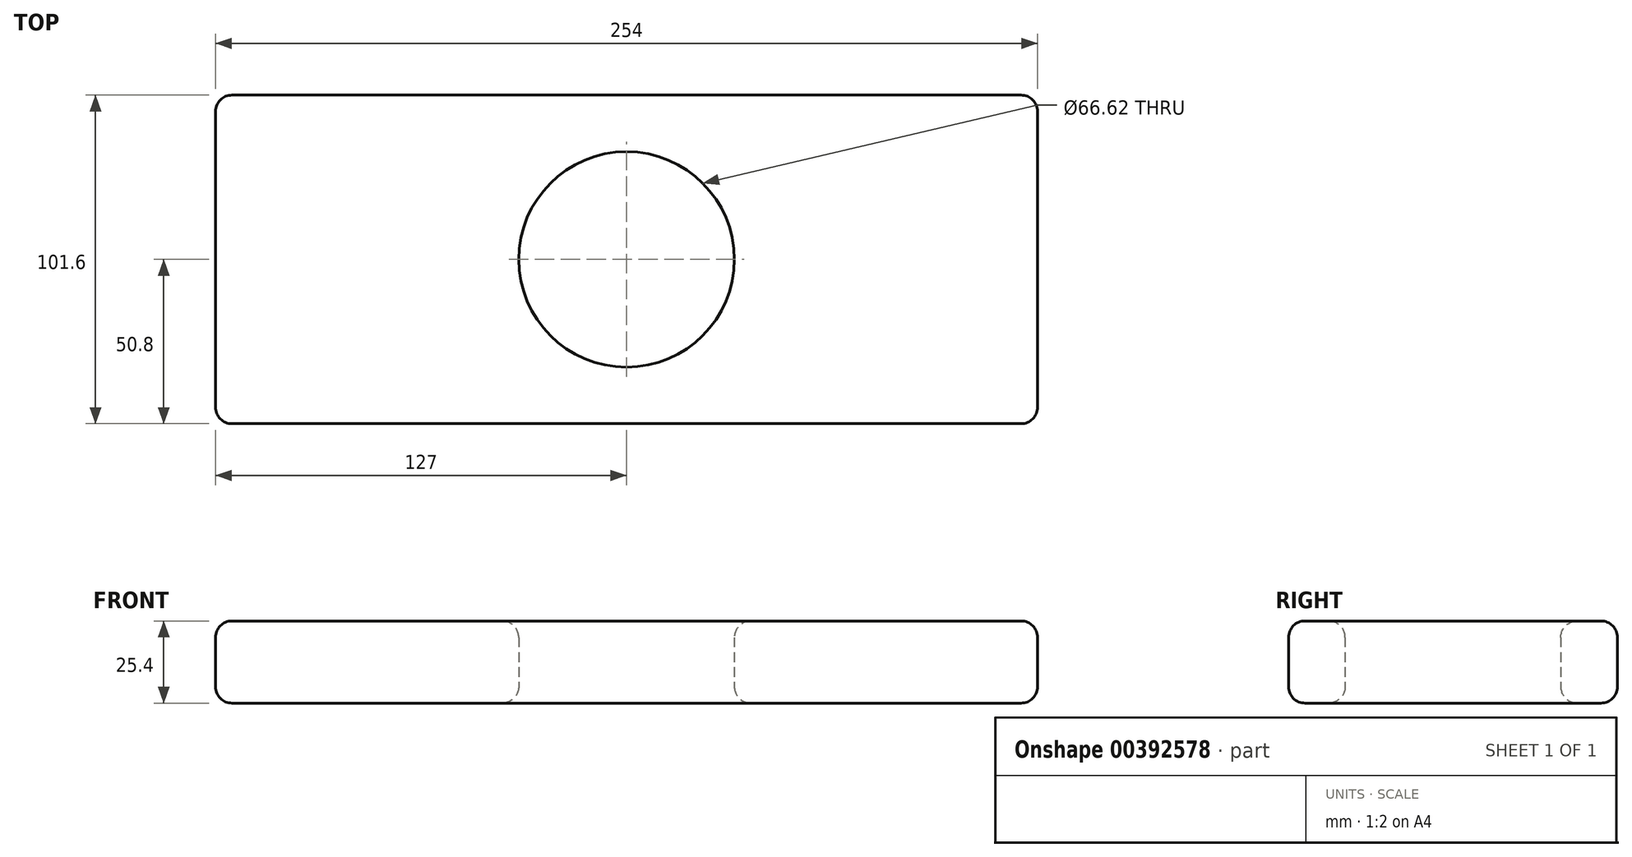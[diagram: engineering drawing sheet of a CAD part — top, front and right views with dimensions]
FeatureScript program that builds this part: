
annotation { "Feature Type Name" : "Feature", "Feature Type Description" : "" }
export const myFeature = defineFeature(function(context is Context, id is Id, definition is map)
    precondition{}
    {
        {
            var Q0;
            Q0=qCreatedBy(makeId("Top.planeOp"),FACE);
            var sketch = newSketch(context, id + "F0", { "sketchPlane" : qUnion([Q0])});
            skLineSegment(sketch, "E0.bottom", {"start": v(-127, 50.8) * mm, "end": v(127, 50.8) * mm});
            skLineSegment(sketch, "E0.top", {"start": v(-127, -50.8) * mm, "end": v(127, -50.8) * mm});
            skLineSegment(sketch, "E0.left", {"start": v(-127, 50.8) * mm, "end": v(-127, -50.8) * mm});
            skLineSegment(sketch, "E0.right", {"start": v(127, 50.8) * mm, "end": v(127, -50.8) * mm});
            skPoint(sketch, "E0.middle", {"position": v(0, 0) * mm});
            skCircle(sketch, "E1", {"center": v(0, 0) * mm, "radius": 33.31 * mm});
            skSolve(sketch);
        }
        {
            var Q0;
            Q0=makeQuery(id+"F0.imprint","IMPRINT",FACE,{"disambiguationData":[TD([[makeQuery(id+"F0.imprint","IMPRINT",EDGE,{"derivedFrom":sQuery(id+"F0.wireOp",EDGE,"E0.bottom")}),-1.0]])]});
            extrude(context, id + "F1", {"entities" : qUnion([Q0]), "endBound" : BoundingType.SYMMETRIC, "depth" : 25.4 * mm});
        }
        {
            var Q0;
            Q0=makeQuery(id+"F1.opExtrude","CAP_EDGE",EDGE,{"disambiguationData":[OSD([sQuery(id+"F0.wireOp",EDGE,"E1")])],"isStart":false});
            fillet(context, id + "F2", {"entities" : qUnion([Q0]), "radius" : 5.08 * mm, "tangentPropagation" : true, "allowEdgeOverflow" : false});
        }
        {
            var Q0;
            Q0=makeQuery(id+"F1.opExtrude","CAP_EDGE",EDGE,{"disambiguationData":[OSD([sQuery(id+"F0.wireOp",EDGE,"E0.top")])],"isStart":false});
            var Q1;
            Q1=makeQuery(id+"F1.opExtrude","CAP_EDGE",EDGE,{"disambiguationData":[OSD([sQuery(id+"F0.wireOp",EDGE,"E0.bottom")])],"isStart":false});
            var Q2;
            Q2=makeQuery(id+"F1.opExtrude","CAP_EDGE",EDGE,{"disambiguationData":[OSD([sQuery(id+"F0.wireOp",EDGE,"E0.left")])],"isStart":false});
            var Q3;
            Q3=makeQuery(id+"F1.opExtrude","CAP_EDGE",EDGE,{"disambiguationData":[OSD([sQuery(id+"F0.wireOp",EDGE,"E0.right")])],"isStart":false});
            var Q4;
            Q4=makeQuery(id+"F1.opExtrude","SWEPT_EDGE",EDGE,{"disambiguationData":[OSD([sQuery(id+"F0.wireOp",EDGE,"E0.bottom"),sQuery(id+"F0.wireOp",EDGE,"E0.right")])]});
            var Q5;
            Q5=makeQuery(id+"F1.opExtrude","CAP_EDGE",EDGE,{"disambiguationData":[OSD([sQuery(id+"F0.wireOp",EDGE,"E0.right")])],"isStart":true});
            var Q6;
            Q6=makeQuery(id+"F1.opExtrude","CAP_EDGE",EDGE,{"disambiguationData":[OSD([sQuery(id+"F0.wireOp",EDGE,"E0.bottom")])],"isStart":true});
            var Q7;
            Q7=makeQuery(id+"F1.opExtrude","CAP_EDGE",EDGE,{"disambiguationData":[OSD([sQuery(id+"F0.wireOp",EDGE,"E0.top")])],"isStart":true});
            var Q8;
            Q8=makeQuery(id+"F1.opExtrude","CAP_EDGE",EDGE,{"disambiguationData":[OSD([sQuery(id+"F0.wireOp",EDGE,"E1")])],"isStart":true});
            var Q9;
            Q9=makeQuery(id+"F1.opExtrude","SWEPT_EDGE",EDGE,{"disambiguationData":[OSD([sQuery(id+"F0.wireOp",EDGE,"E0.top"),sQuery(id+"F0.wireOp",EDGE,"E0.right")])]});
            var Q10;
            Q10=makeQuery(id+"F1.opExtrude","SWEPT_EDGE",EDGE,{"disambiguationData":[OSD([sQuery(id+"F0.wireOp",EDGE,"E0.top"),sQuery(id+"F0.wireOp",EDGE,"E0.left")])]});
            var Q11;
            Q11=makeQuery(id+"F1.opExtrude","SWEPT_EDGE",EDGE,{"disambiguationData":[OSD([sQuery(id+"F0.wireOp",EDGE,"E0.bottom"),sQuery(id+"F0.wireOp",EDGE,"E0.left")])]});
            var Q12;
            Q12=makeQuery(id+"F1.opExtrude","CAP_EDGE",EDGE,{"disambiguationData":[OSD([sQuery(id+"F0.wireOp",EDGE,"E0.left")])],"isStart":true});
            fillet(context, id + "F3", {"entities" : qUnion([Q0, Q1, Q2, Q3, Q4, Q5, Q6, Q7, Q8, Q9, Q10, Q11, Q12]), "radius" : 5.08 * mm, "tangentPropagation" : true, "allowEdgeOverflow" : false});
        }
    });
